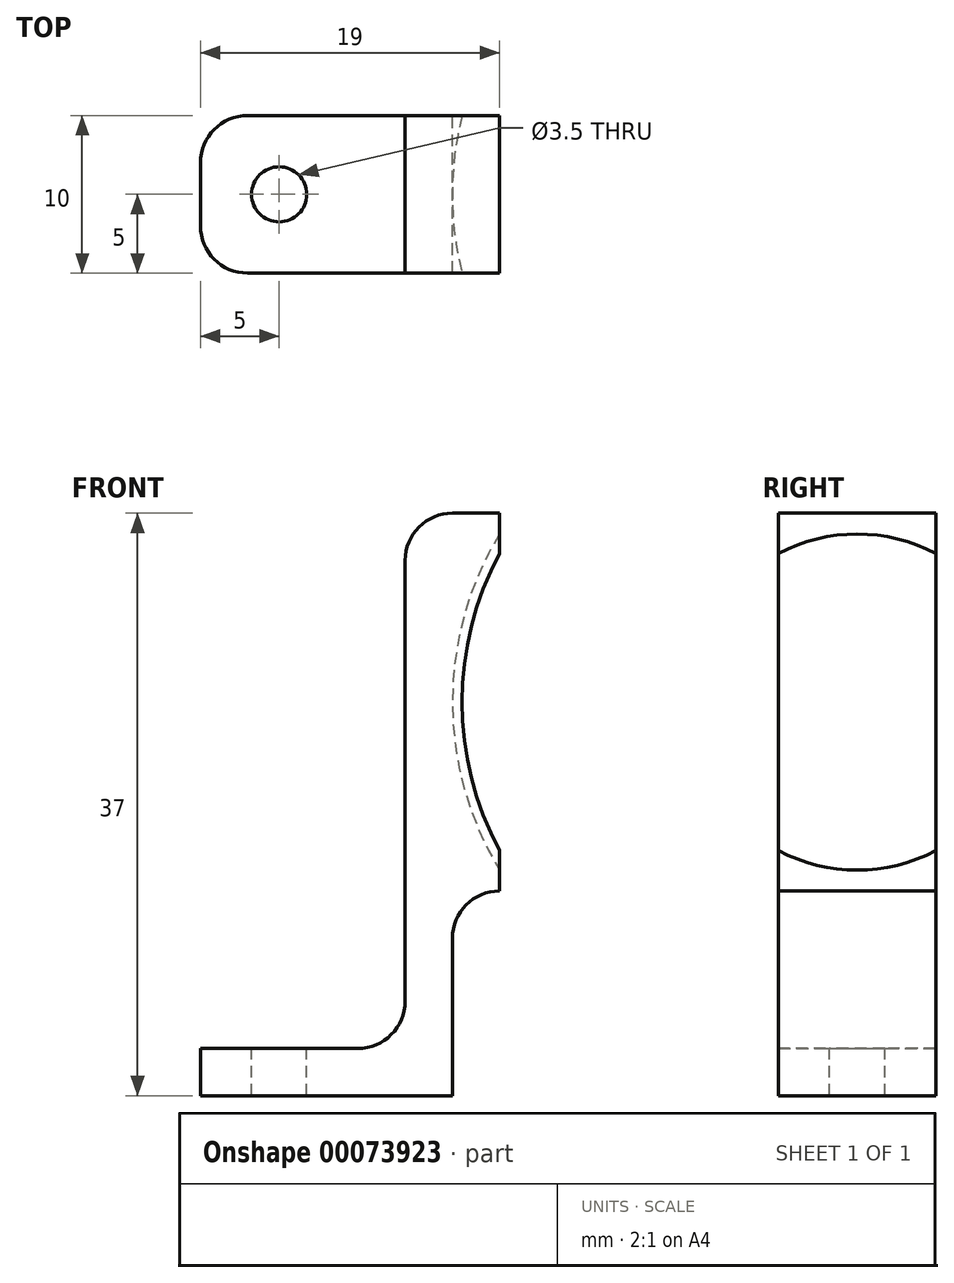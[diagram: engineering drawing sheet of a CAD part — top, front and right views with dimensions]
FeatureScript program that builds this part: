
annotation { "Feature Type Name" : "Feature", "Feature Type Description" : "" }
export const myFeature = defineFeature(function(context is Context, id is Id, definition is map)
    precondition{}
    {
        {
            var Q0;
            Q0=qCreatedBy(makeId("Front.planeOp"),FACE);
            var sketch = newSketch(context, id + "F0", { "sketchPlane" : qUnion([Q0])});
            skArc(sketch, "E0", {"start": v(0, 20.5) * mm, "mid": v(-20.5, 0) * mm, "end": v(0, -20.5) * mm});
            skLineSegment(sketch, "E1", {"start": v(0, -20.5) * mm, "end": v(0, 20.5) * mm});
            skSolve(sketch);
        }
        {
            var Q0;
            Q0=qCreatedBy(makeId("Front.planeOp"),FACE);
            var sketch = newSketch(context, id + "F1", { "sketchPlane" : qUnion([Q0])});
            skLineSegment(sketch, "E2", {"start": v(0, 0) * mm, "end": v(-20.5, 0) * mm});
            skLineSegment(sketch, "E3", {"start": v(-20.5, 0) * mm, "end": v(-20.5, -25) * mm});
            skLineSegment(sketch, "E4", {"start": v(-20.5, 0) * mm, "end": v(-17.5, 0) * mm});
            skLineSegment(sketch, "E5", {"start": v(-17.5, 0) * mm, "end": v(-17.5, 12) * mm});
            skLineSegment(sketch, "E6", {"start": v(-17.5, 0) * mm, "end": v(-17.5, -12) * mm});
            skLineSegment(sketch, "E7", {"start": v(-17.5, -12) * mm, "end": v(-20.5, -12) * mm});
            skLineSegment(sketch, "E8", {"start": v(-17.5, 12) * mm, "end": v(-23.5, 12) * mm});
            skLineSegment(sketch, "E9", {"start": v(-23.5, 12) * mm, "end": v(-23.5, -22) * mm});
            skLineSegment(sketch, "E10", {"start": v(-20.5, -25) * mm, "end": v(-36.5, -25) * mm});
            skLineSegment(sketch, "E11", {"start": v(-36.5, -25) * mm, "end": v(-36.5, -22) * mm});
            skLineSegment(sketch, "E12", {"start": v(-36.5, -22) * mm, "end": v(-23.5, -22) * mm});
            skPoint(sketch, "E13.orphan", {"position": v(-23.5, -25) * mm});
            skSolve(sketch);
        }
        {
            var Q0;
            Q0 = qSketchRegion(id + "F1", true);
            extrude(context, id + "F2", {"entities" : qUnion([Q0]), "depth" : 5 * mm, "hasSecondDirection" : true, "secondDirectionOppositeDirection" : true, "secondDirectionDepth" : 5 * mm});
        }
        {
            var Q0;
            Q0=makeQuery(id+"F0.imprint","IMPRINT",FACE,{"disambiguationData":[TD([[makeQuery(id+"F0.imprint","IMPRINT",EDGE,{"derivedFrom":sQuery(id+"F0.wireOp",EDGE,"E0")}),1.0]])]});
            var Q1;
            Q1=sQuery(id+"F0.wireOp",EDGE,"E1");
            revolve(context, id + "F3", {"operationType" : NewBodyOperationType.REMOVE, "entities" : qUnion([Q0]), "axis" : qUnion([Q1]), "revolveType" : RevolveType.FULL, "oppositeDirection" : true});
        }
        {
            var Q0;
            Q0=makeQuery(id+"F2.opExtrude","SWEPT_EDGE",EDGE,{"disambiguationData":[OSD([sQuery(id+"F1.wireOp",EDGE,"E8"),sQuery(id+"F1.wireOp",EDGE,"E9")])]});
            var Q1;
            Q1=makeQuery(id+"F2.opExtrude","SWEPT_EDGE",EDGE,{"disambiguationData":[OSD([sQuery(id+"F1.wireOp",EDGE,"E9"),sQuery(id+"F1.wireOp",EDGE,"E12")])]});
            fillet(context, id + "F4", {"entities" : qUnion([Q0, Q1]), "radius" : 3 * mm, "tangentPropagation" : true, "allowEdgeOverflow" : false});
        }
        {
            var Q0;
            Q0=makeQuery(id+"F2.opExtrude","SWEPT_EDGE",EDGE,{"disambiguationData":[OSD([sQuery(id+"F1.wireOp",EDGE,"E3"),sQuery(id+"F1.wireOp",EDGE,"E7")])]});
            fillet(context, id + "F5", {"entities" : qUnion([Q0]), "radius" : 3 * mm, "tangentPropagation" : true, "allowEdgeOverflow" : false});
        }
        {
            var Q0;
            Q0=makeQuery(id+"F2.opExtrude","SWEPT_FACE",FACE,{"disambiguationData":[OSD([sQuery(id+"F1.wireOp",EDGE,"E12")])]});
            var sketch = newSketch(context, id + "F6", { "sketchPlane" : qUnion([Q0])});
            skLineSegment(sketch, "E14", {"start": v(-36.5, 5) * mm, "end": v(-26.5, -5) * mm});
            skCircle(sketch, "E15", {"center": v(-31.5, 0) * mm, "radius": 1.75 * mm});
            skSolve(sketch);
        }
        {
            var Q0;
            Q0 = qSketchRegion(id + "F6", true);
            extrude(context, id + "F7", {"entities" : qUnion([Q0]), "operationType" : NewBodyOperationType.REMOVE, "oppositeDirection" : true, "depth" : 25 * mm});
        }
        {
            var Q0;
            Q0=makeQuery(id+"F2.opExtrude","CAP_EDGE",EDGE,{"disambiguationData":[OSD([sQuery(id+"F1.wireOp",EDGE,"E11")])],"isStart":false});
            var Q1;
            Q1=makeQuery(id+"F2.opExtrude","CAP_EDGE",EDGE,{"disambiguationData":[OSD([sQuery(id+"F1.wireOp",EDGE,"E11")])],"isStart":true});
            fillet(context, id + "F8", {"entities" : qUnion([Q0, Q1]), "radius" : 3 * mm, "tangentPropagation" : true, "allowEdgeOverflow" : false});
        }
    });
